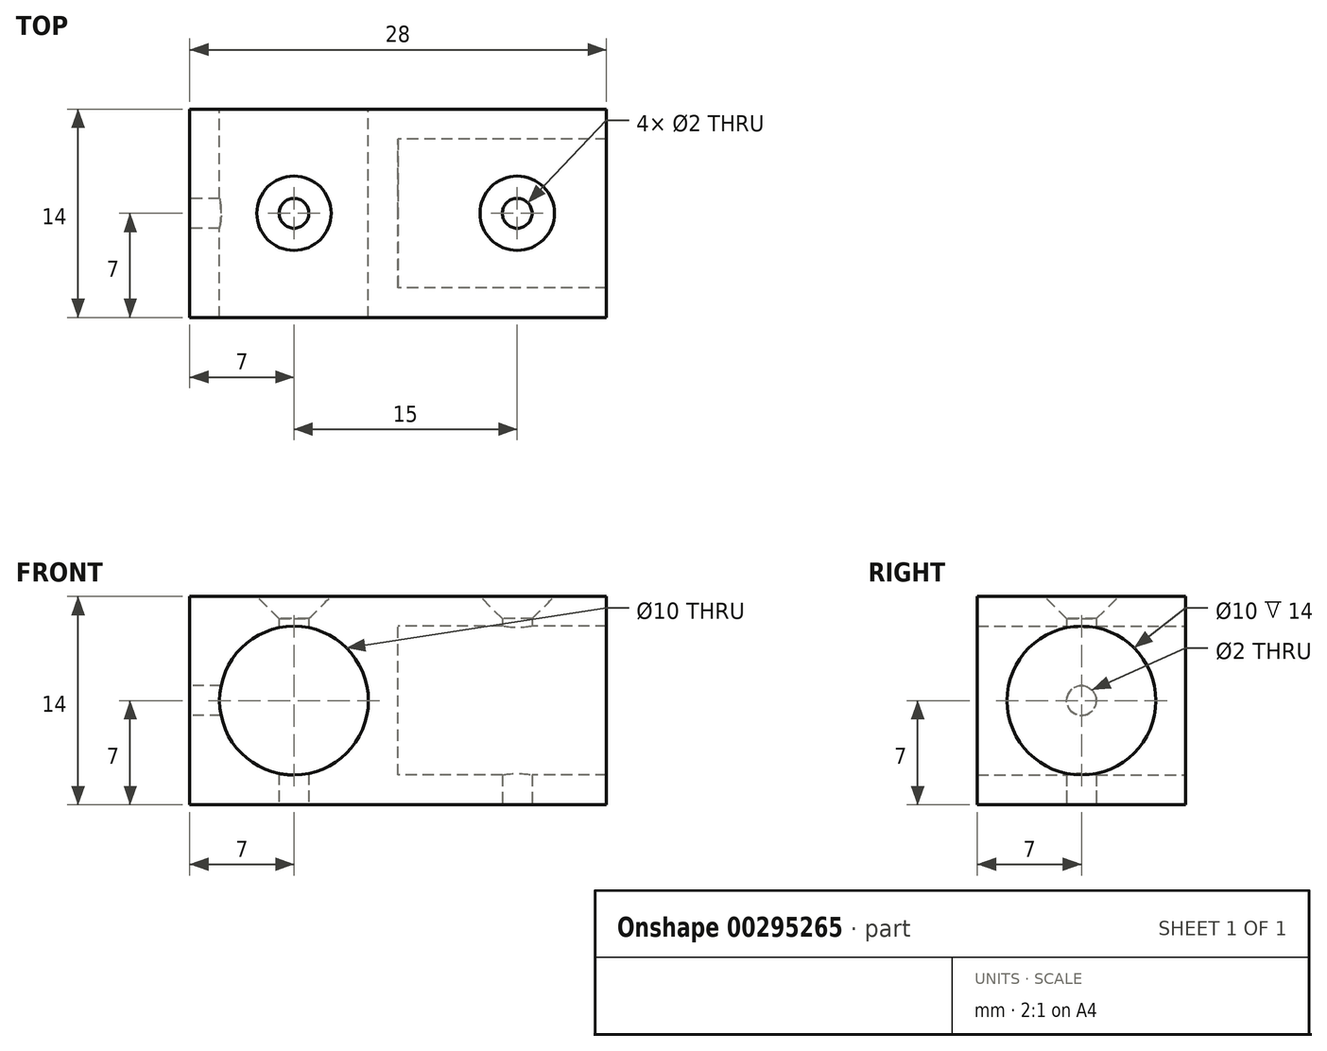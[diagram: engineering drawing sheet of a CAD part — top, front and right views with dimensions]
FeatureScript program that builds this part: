
annotation { "Feature Type Name" : "Feature", "Feature Type Description" : "" }
export const myFeature = defineFeature(function(context is Context, id is Id, definition is map)
    precondition{}
    {
        {
            assignVariable(context, id + "F0", {"name" : "diameter", "anyValue" : 10 * mm});
        }
        {
            assignVariable(context, id + "F1", {"name" : "border", "anyValue" : 2 * mm});
        }
        {
            var Q0;
            Q0=qCreatedBy(makeId("Front.planeOp"),FACE);
            var sketch = newSketch(context, id + "F2", { "sketchPlane" : qUnion([Q0])});
            skLineSegment(sketch, "E0.bottom", {"start": v(-7, 7) * mm, "end": v(7, 7) * mm});
            skLineSegment(sketch, "E0.top", {"start": v(-7, -7) * mm, "end": v(7, -7) * mm});
            skLineSegment(sketch, "E0.left", {"start": v(-7, 7) * mm, "end": v(-7, -7) * mm});
            skLineSegment(sketch, "E0.right", {"start": v(7, 7) * mm, "end": v(7, -7) * mm});
            skPoint(sketch, "E0.middle", {"position": v(0, 0) * mm});
            skCircle(sketch, "E1", {"center": v(0, 0) * mm, "radius": 5 * mm});
            skSolve(sketch);
        }
        {
            var Q0;
            Q0=makeQuery(id+"F2.imprint","IMPRINT",FACE,{"disambiguationData":[TD([[makeQuery(id+"F2.imprint","IMPRINT",EDGE,{"derivedFrom":sQuery(id+"F2.wireOp",EDGE,"E0.bottom")}),-1.0]])]});
            extrude(context, id + "F3", {"entities" : qUnion([Q0]), "depth" : getVariable(context, 'diameter') + 2 * getVariable(context, 'border')});
        }
        {
            var Q0;
            Q0=makeQuery(id+"F3.opExtrude","SWEPT_BODY",BODY,{"disambiguationData":[OSD([sQuery(id+"F2.wireOp",EDGE,"E0.bottom"),sQuery(id+"F2.wireOp",EDGE,"E0.top"),sQuery(id+"F2.wireOp",EDGE,"E0.left"),sQuery(id+"F2.wireOp",EDGE,"E0.right"),sQuery(id+"F2.wireOp",EDGE,"E1")])]});
            var Q1;
            Q1=sQuery(id+"F2.wireOp",EDGE,"E0.right");
            transform(context, id + "F4", {"entities" : qUnion([Q0]), "transformType" : TransformType.ROTATION, "transformAxis" : qUnion([Q1]), "angle" : 90 * degree, "oppositeDirection" : true, "makeCopy" : true});
        }
        {
            var Q0;
            Q0=makeQuery(id+"F3.opExtrude","SWEPT_BODY",BODY,{"disambiguationData":[OSD([sQuery(id+"F2.wireOp",EDGE,"E0.bottom"),sQuery(id+"F2.wireOp",EDGE,"E0.top"),sQuery(id+"F2.wireOp",EDGE,"E0.left"),sQuery(id+"F2.wireOp",EDGE,"E0.right"),sQuery(id+"F2.wireOp",EDGE,"E1")])]});
            var Q1;
            Q1=makeQuery(id+"F4.opPattern","COPY",BODY,{"derivedFrom":makeQuery(id+"F3.opExtrude","SWEPT_BODY",BODY,{"disambiguationData":[OSD([sQuery(id+"F2.wireOp",EDGE,"E0.bottom"),sQuery(id+"F2.wireOp",EDGE,"E0.top"),sQuery(id+"F2.wireOp",EDGE,"E0.left"),sQuery(id+"F2.wireOp",EDGE,"E0.right"),sQuery(id+"F2.wireOp",EDGE,"E1")])]}),"instanceName":"1"});
            booleanBodies(context, id + "F5", {"operationType" : BooleanOperationType.UNION, "tools" : qUnion([Q0, Q1])});
        }
        {
            var Q0;
            Q0=makeQuery(id+"Fl3ljRVsUfp6X2e_1.boolean.opBoolean","MERGE",FACE,{"derivedFrom":[makeQuery(id+"F3.opExtrude","SWEPT_FACE",FACE,{"disambiguationData":[OSD([sQuery(id+"F2.wireOp",EDGE,"E0.top")])]}),makeQuery(id+"Fl3ljRVsUfp6X2e_1.opExtrude","SWEPT_FACE",FACE,{"disambiguationData":[OSD([sQuery(id+"FVMD0OYcA93SlPO_1.wireOp",EDGE,"awNTX10d-obja-QDea-18vj-DRB82mjigwJT.bottom")])]})]});
            var sketch = newSketch(context, id + "F6", { "sketchPlane" : qUnion([Q0])});
            skCircle(sketch, "E2", {"center": v(0, 7) * mm, "radius": 1 * mm});
            skCircle(sketch, "E3", {"center": v(15, 7) * mm, "radius": 1 * mm});
            skSolve(sketch);
        }
        {
            var Q0;
            Q0=makeQuery(id+"F3.opExtrude","SWEPT_FACE",FACE,{"disambiguationData":[OSD([sQuery(id+"F2.wireOp",EDGE,"E0.left")])]});
            var sketch = newSketch(context, id + "F7", { "sketchPlane" : qUnion([Q0])});
            skCircle(sketch, "E4", {"center": v(7, 0) * mm, "radius": 1 * mm});
            skPoint(sketch, "E4.centerSnap0", {"position": v(7, 7) * mm});
            skSolve(sketch);
        }
        {
            var Q0;
            Q0 = qSketchRegion(id + "F6", true);
            extrude(context, id + "F8", {"entities" : qUnion([Q0]), "operationType" : NewBodyOperationType.REMOVE, "endBound" : BoundingType.THROUGH_ALL, "oppositeDirection" : true, "depth" : 25 * mm});
        }
        {
            var Q0;
            Q0=makeQuery(id+"F7.imprint","IMPRINT",FACE,{"disambiguationData":[TD([[makeQuery(id+"F7.imprint","IMPRINT",EDGE,{"derivedFrom":sQuery(id+"F7.wireOp",EDGE,"E4")}),1.0]])]});
            extrude(context, id + "F9", {"entities" : qUnion([Q0]), "operationType" : NewBodyOperationType.REMOVE, "endBound" : BoundingType.UP_TO_NEXT, "oppositeDirection" : true, "depth" : 25 * mm});
        }
        {
            var Q0;
            Q0=makeQuery(id+"F8.boolean.opBoolean","COPY",EDGE,{"derivedFrom":makeQuery(id+"F8.opExtrude","CAP_EDGE",EDGE,{"disambiguationData":[OSD([sQuery(id+"F6.wireOp",EDGE,"E2")])],"isStart":true})});
            var Q1;
            Q1=makeQuery(id+"F8.boolean.opBoolean","COPY",EDGE,{"derivedFrom":makeQuery(id+"F8.opExtrude","CAP_EDGE",EDGE,{"disambiguationData":[OSD([sQuery(id+"F6.wireOp",EDGE,"E3")])],"isStart":true})});
            var Q2;
            {var subQ0=makeQuery(id+"F3.opExtrude","SWEPT_FACE",FACE,{"disambiguationData":[OSD([sQuery(id+"F2.wireOp",EDGE,"E0.bottom")])]});Q2=makeQuery(id+"F8.boolean.opBoolean","INTERSECT",EDGE,{"derivedFrom":[makeQuery(id+"F5.opBoolean","MERGE",FACE,{"derivedFrom":[subQ0,makeQuery(id+"F4.opPattern","COPY",FACE,{"derivedFrom":subQ0,"instanceName":"1"})]}),makeQuery(id+"F8.opExtrude","SWEPT_FACE",FACE,{"disambiguationData":[OSD([sQuery(id+"F6.wireOp",EDGE,"E2")])]})]});}
            var Q3;
            {var subQ0=makeQuery(id+"F3.opExtrude","SWEPT_FACE",FACE,{"disambiguationData":[OSD([sQuery(id+"F2.wireOp",EDGE,"E0.bottom")])]});Q3=makeQuery(id+"F8.boolean.opBoolean","INTERSECT",EDGE,{"derivedFrom":[makeQuery(id+"F5.opBoolean","MERGE",FACE,{"derivedFrom":[subQ0,makeQuery(id+"F4.opPattern","COPY",FACE,{"derivedFrom":subQ0,"instanceName":"1"})]}),makeQuery(id+"F8.opExtrude","SWEPT_FACE",FACE,{"disambiguationData":[OSD([sQuery(id+"F6.wireOp",EDGE,"E3")])]})]});}
            var Q4;
            Q4=makeQuery(id+"F9.boolean.opBoolean","COPY",EDGE,{"derivedFrom":makeQuery(id+"F9.opExtrude","CAP_EDGE",EDGE,{"disambiguationData":[OSD([sQuery(id+"F7.wireOp",EDGE,"E4")])],"isStart":true})});
            chamfer(context, id + "F10", {"entities" : qUnion([Q0, Q1, Q2, Q3, Q4]), "chamferType" : ChamferType.OFFSET_ANGLE, "width" : ((5 - 2) / 2) * mm, "oppositeDirection" : false, "angle" : 45 * degree, "tangentPropagation" : true});
        }
    });
